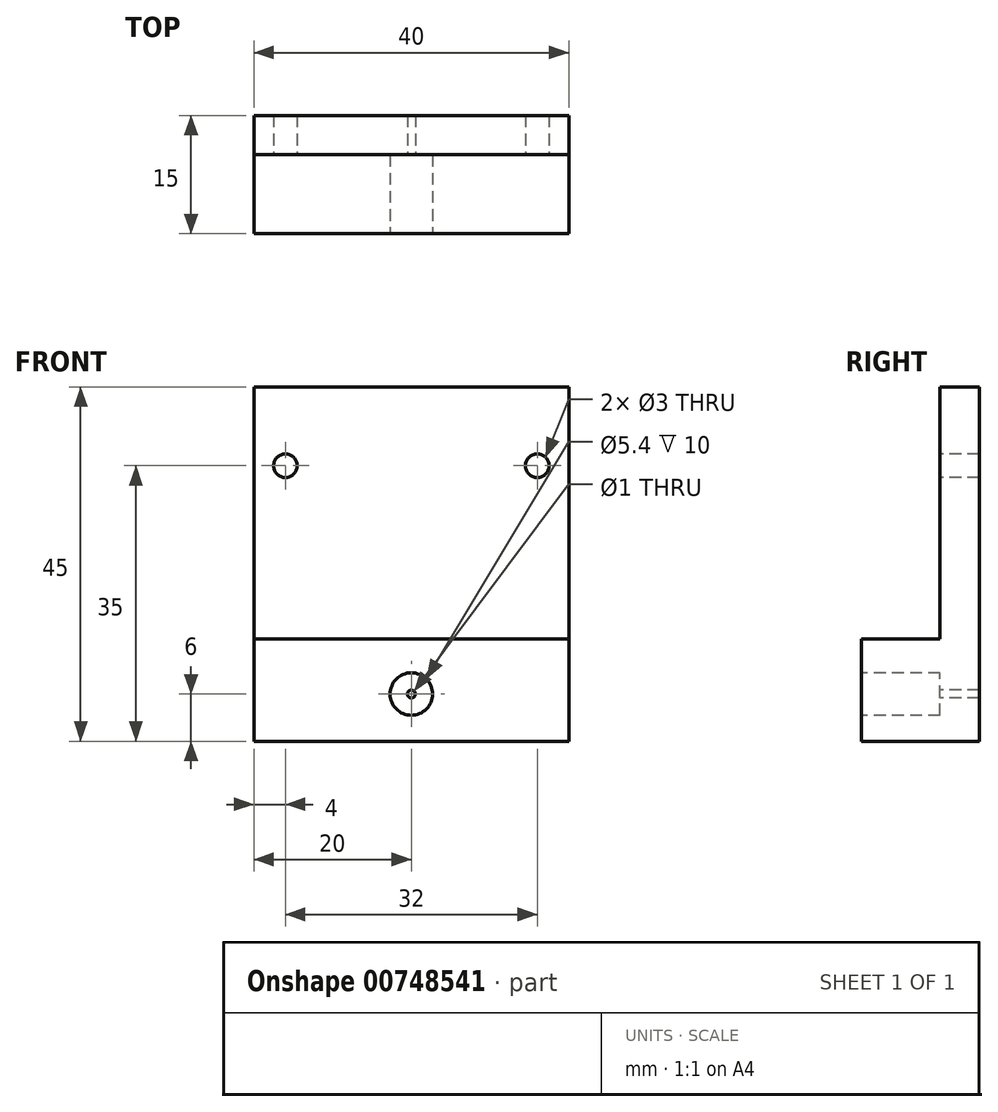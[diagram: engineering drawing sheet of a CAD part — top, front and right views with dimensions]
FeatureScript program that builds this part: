
annotation { "Feature Type Name" : "Feature", "Feature Type Description" : "" }
export const myFeature = defineFeature(function(context is Context, id is Id, definition is map)
    precondition{}
    {
        {
            var Q0;
            Q0=qCreatedBy(makeId("Front.planeOp"),FACE);
            var sketch = newSketch(context, id + "F0", { "sketchPlane" : qUnion([Q0])});
            skLineSegment(sketch, "E0.bottom", {"start": v(-20, 22.5) * mm, "end": v(20, 22.5) * mm});
            skLineSegment(sketch, "E0.top", {"start": v(-20, -22.5) * mm, "end": v(20, -22.5) * mm});
            skLineSegment(sketch, "E0.left", {"start": v(-20, 22.5) * mm, "end": v(-20, -22.5) * mm});
            skLineSegment(sketch, "E0.right", {"start": v(20, 22.5) * mm, "end": v(20, -22.5) * mm});
            skPoint(sketch, "E0.middle", {"position": v(0, 0) * mm});
            skSolve(sketch);
        }
        {
            var Q0;
            Q0=makeQuery(id+"F0.imprint","IMPRINT",FACE,{"disambiguationData":[TD([[makeQuery(id+"F0.imprint","IMPRINT",EDGE,{"derivedFrom":sQuery(id+"F0.wireOp",EDGE,"E0.bottom")}),-1.0]])]});
            extrude(context, id + "F1", {"entities" : qUnion([Q0]), "depth" : 15 * mm, "offsetDistance" : 25 * mm});
        }
        {
            var Q0;
            Q0=makeQuery(id+"F1.opExtrude","CAP_FACE",FACE,{"disambiguationData":[OSD([sQuery(id+"F0.wireOp",EDGE,"E0.bottom"),sQuery(id+"F0.wireOp",EDGE,"E0.top"),sQuery(id+"F0.wireOp",EDGE,"E0.left"),sQuery(id+"F0.wireOp",EDGE,"E0.right")])],"isStart":false});
            var sketch = newSketch(context, id + "F2", { "sketchPlane" : qUnion([Q0])});
            skCircle(sketch, "E1", {"center": v(16, 12.5) * mm, "radius": 1.5 * mm});
            skCircle(sketch, "E2", {"center": v(-16, 12.5) * mm, "radius": 1.5 * mm});
            skSolve(sketch);
        }
        {
            var Q0;
            Q0=qSketchRegion(id+"F2",true);
            extrude(context, id + "F3", {"entities" : qUnion([Q0]), "operationType" : NewBodyOperationType.REMOVE, "oppositeDirection" : true, "depth" : 25 * mm, "offsetDistance" : 25 * mm});
        }
        {
            var Q0;
            {var subQ1=sQuery(id+"F0.wireOp",EDGE,"E0.left");var subQ3=sQuery(id+"F0.wireOp",EDGE,"E0.bottom");Q0=makeQuery(id+"FwaKjzzbafGnsFd_1.boolean.opBoolean","SPLIT",FACE,{"disambiguationData":[TD([makeQuery(id+"F1.opExtrude","SWEPT_FACE",FACE,{"disambiguationData":[OSD([subQ1])]})])],"derivedFrom":makeQuery(id+"F1.opExtrude","SWEPT_FACE",FACE,{"disambiguationData":[OSD([subQ3])]})});}
            var sketch = newSketch(context, id + "F4", { "sketchPlane" : qUnion([Q0])});
            skPoint(sketch, "E3.centerSnap0", {"position": v(-20, -7.5) * mm});
            skPoint(sketch, "E4", {"position": v(-16, -7.5) * mm});
            skPoint(sketch, "E5", {"position": v(16, -7.5) * mm});
            skSolve(sketch);
        }
        {
            var Q0;
            Q0=makeQuery(id+"F1.opExtrude","CAP_FACE",FACE,{"disambiguationData":[OSD([sQuery(id+"F0.wireOp",EDGE,"E0.bottom"),sQuery(id+"F0.wireOp",EDGE,"E0.top"),sQuery(id+"F0.wireOp",EDGE,"E0.left"),sQuery(id+"F0.wireOp",EDGE,"E0.right")])],"isStart":false});
            var sketch = newSketch(context, id + "F5", { "sketchPlane" : qUnion([Q0])});
            skCircle(sketch, "E6.cCircle", {"center": v(0, 22.5) * mm, "radius": 0.1 * mm, "construction": true});
            skLineSegment(sketch, "E6.0", {"start": v(-0.17, 22.6) * mm, "end": v(0.17, 22.6) * mm});
            skLineSegment(sketch, "E6.1", {"start": v(0.17, 22.6) * mm, "end": v(0, 22.3) * mm});
            skLineSegment(sketch, "E6.2", {"start": v(0, 22.3) * mm, "end": v(-0.17, 22.6) * mm});
            skPoint(sketch, "E6.0.midPoint", {"position": v(0, 22.6) * mm});
            skSolve(sketch);
        }
        {
            var Q0;
            {var subQ0=sQuery(id+"F0.wireOp",EDGE,"E0.bottom");Q0=makeQuery(id+"F4.imprint","IMPRINT",FACE,{"disambiguationData":[TD([[makeQuery(id+"F4.imprint","IMPRINT",EDGE,{"derivedFrom":makeQuery(id+"F1.opExtrude","CAP_EDGE",EDGE,{"disambiguationData":[OSD([subQ0])],"isStart":true})}),-1.0]])]});}
            var sketch = newSketch(context, id + "F6", { "sketchPlane" : qUnion([Q0])});
            skCircle(sketch, "E7", {"center": v(16, -12.5) * mm, "radius": 1 * mm});
            skCircle(sketch, "E8", {"center": v(-16, -12.5) * mm, "radius": 1 * mm});
            skSolve(sketch);
        }
        {
            var Q0;
            Q0=makeQuery(id+"F1.opExtrude","CAP_FACE",FACE,{"disambiguationData":[OSD([sQuery(id+"F0.wireOp",EDGE,"E0.bottom"),sQuery(id+"F0.wireOp",EDGE,"E0.top"),sQuery(id+"F0.wireOp",EDGE,"E0.left"),sQuery(id+"F0.wireOp",EDGE,"E0.right")])],"isStart":false});
            var sketch = newSketch(context, id + "F7", { "sketchPlane" : qUnion([Q0])});
            skCircle(sketch, "E9", {"center": v(0, -16.5) * mm, "radius": 2.7 * mm});
            skSolve(sketch);
        }
        {
            var Q0;
            Q0=qSketchRegion(id+"F7",true);
            extrude(context, id + "F8", {"entities" : qUnion([Q0]), "operationType" : NewBodyOperationType.REMOVE, "oppositeDirection" : true, "depth" : 10 * mm, "offsetDistance" : 25 * mm});
        }
        {
            var Q0;
            Q0=makeQuery(id+"F5.imprint","IMPRINT",FACE,{"disambiguationData":[TD([[makeQuery(id+"F5.imprint","IMPRINT",EDGE,{"derivedFrom":makeQuery(id+"F1.opExtrude","CAP_EDGE",EDGE,{"disambiguationData":[OSD([sQuery(id+"F0.wireOp",EDGE,"E0.top")])],"isStart":false})}),1.0]])]});
            var sketch = newSketch(context, id + "F9", { "sketchPlane" : qUnion([Q0])});
            skLineSegment(sketch, "E10.bottom", {"start": v(-20, 22.5) * mm, "end": v(20, 22.5) * mm});
            skLineSegment(sketch, "E10.top", {"start": v(-20, -9.5) * mm, "end": v(20, -9.5) * mm});
            skLineSegment(sketch, "E10.left", {"start": v(-20, 22.5) * mm, "end": v(-20, -9.5) * mm});
            skLineSegment(sketch, "E10.right", {"start": v(20, 22.5) * mm, "end": v(20, -9.5) * mm});
            skPoint(sketch, "E10.middle", {"position": v(0, 6.5) * mm});
            skSolve(sketch);
        }
        {
            var Q0;
            Q0 = qSketchRegion(id + "F9", true);
            extrude(context, id + "F10", {"entities" : qUnion([Q0]), "operationType" : NewBodyOperationType.REMOVE, "oppositeDirection" : true, "depth" : 10 * mm, "offsetDistance" : 25 * mm});
        }
        {
            var Q0;
            Q0=makeQuery(id+"F5.imprint","IMPRINT",FACE,{"disambiguationData":[TD([[makeQuery(id+"F5.imprint","IMPRINT",EDGE,{"derivedFrom":makeQuery(id+"F1.opExtrude","CAP_EDGE",EDGE,{"disambiguationData":[OSD([sQuery(id+"F0.wireOp",EDGE,"E0.top")])],"isStart":false})}),1.0]])]});
            var sketch = newSketch(context, id + "F11", { "sketchPlane" : qUnion([Q0])});
            skCircle(sketch, "E11", {"center": v(0, -16.5) * mm, "radius": 0.5 * mm});
            skSolve(sketch);
        }
        {
            var Q0;
            Q0=makeQuery(id+"F11.imprint","IMPRINT",FACE,{"disambiguationData":[TD([[makeQuery(id+"F11.imprint","IMPRINT",EDGE,{"derivedFrom":sQuery(id+"F11.wireOp",EDGE,"E11")}),1.0]])]});
            extrude(context, id + "F12", {"entities" : qUnion([Q0]), "operationType" : NewBodyOperationType.REMOVE, "oppositeDirection" : true, "depth" : 15 * mm, "offsetDistance" : 25 * mm});
        }
    });
